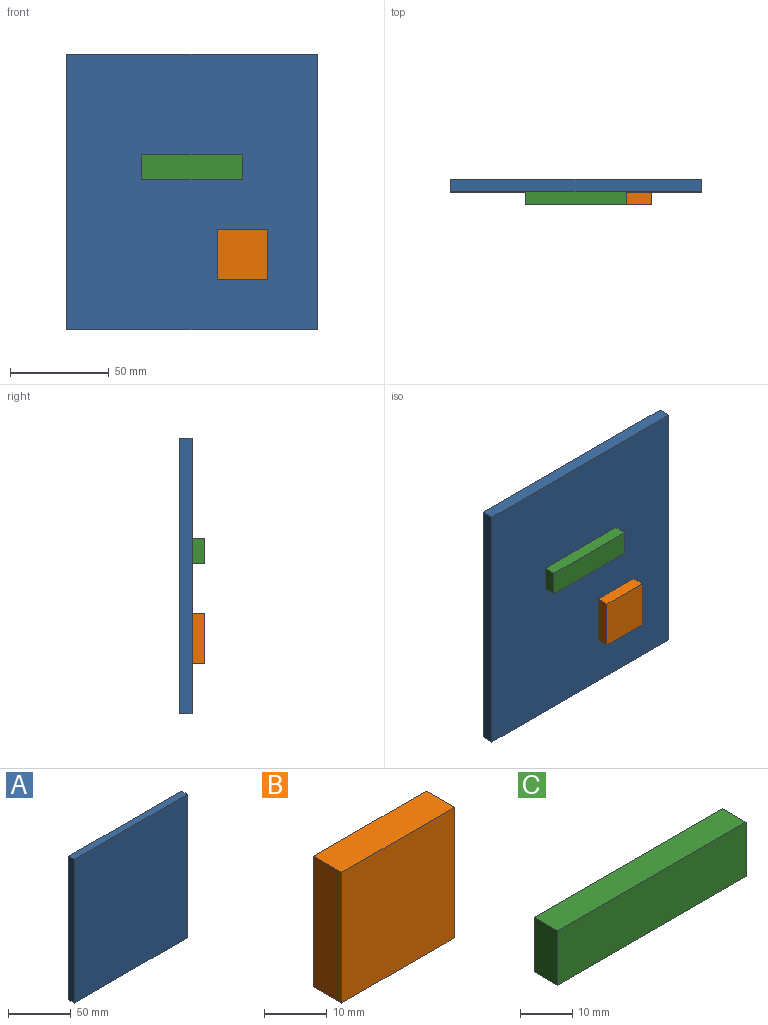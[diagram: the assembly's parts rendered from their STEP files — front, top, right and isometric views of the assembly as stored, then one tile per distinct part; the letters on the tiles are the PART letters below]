
ASSEMBLY  parts=3 mates=2
PART A: 6 faces, bbox 127x6.4x139.7 mm
  f0: plane 139.7x6.35mm, normal (1,0,0), area 887.1mm2, adj f1,f3,f4,f5
  f1: plane 127x6.35mm, normal (0,0,1), area 806.5mm2, adj f0,f2,f4,f5
  f2: plane 139.7x6.35mm, normal (-1,0,0), area 887.1mm2, adj f1,f3,f4,f5
  f3: plane 127x6.35mm, normal (0,0,-1), area 806.5mm2, adj f0,f2,f4,f5
  f4: plane 139.7x127mm, normal (0,-1,0), area 17741.9mm2, adj f0,f1,f2,f3
  f5: plane 139.7x127mm, normal (0,1,0), area 17741.9mm2, adj f0,f1,f2,f3
PART B: 6 faces, bbox 25.4x6.4x25.4 mm
  f0: plane 25.4x6.35mm, normal (1,0,0), area 161.3mm2, adj f1,f3,f4,f5
  f1: plane 25.4x6.35mm, normal (0,0,1), area 161.3mm2, adj f0,f2,f4,f5
  f2: plane 25.4x6.35mm, normal (-1,0,0), area 161.3mm2, adj f1,f3,f4,f5
  f3: plane 25.4x6.35mm, normal (0,0,-1), area 161.3mm2, adj f0,f2,f4,f5
  f4: plane 25.4x25.4mm, normal (0,1,0), area 645.2mm2, adj f0,f1,f2,f3
  f5: plane 25.4x25.4mm, normal (0,-1,0), area 645.2mm2, adj f0,f1,f2,f3
PART C: 6 faces, bbox 50.8x6.4x12.7 mm
  f0: plane 12.7x6.35mm, normal (1,0,0), area 80.6mm2, adj f1,f3,f4,f5
  f1: plane 50.8x6.35mm, normal (0,0,1), area 322.6mm2, adj f0,f2,f4,f5
  f2: plane 12.7x6.35mm, normal (-1,0,0), area 80.6mm2, adj f1,f3,f4,f5
  f3: plane 50.8x6.35mm, normal (0,0,-1), area 322.6mm2, adj f0,f2,f4,f5
  f4: plane 50.8x12.7mm, normal (0,1,0), area 645.2mm2, adj f0,f1,f2,f3
  f5: plane 50.8x12.7mm, normal (0,-1,0), area 645.2mm2, adj f0,f1,f2,f3
PLACE A t=(65.27,6.35,-21.2)mm
PLACE B rot(axis=(1,0,0),180deg) t=(65.27,-6.35,-42.3)mm
PLACE C rot(axis=(0,0,1),180deg) t=(-65.27,-6.35,-21.2)mm
MATE fastened B.f5 <-> A.f4  axis (0,1,0) through (38.1,0,-44.45)mm
MATE fastened A.f4 <-> C.f5  axis (0,-1,0) through (-63.5,0,69.85)mm
